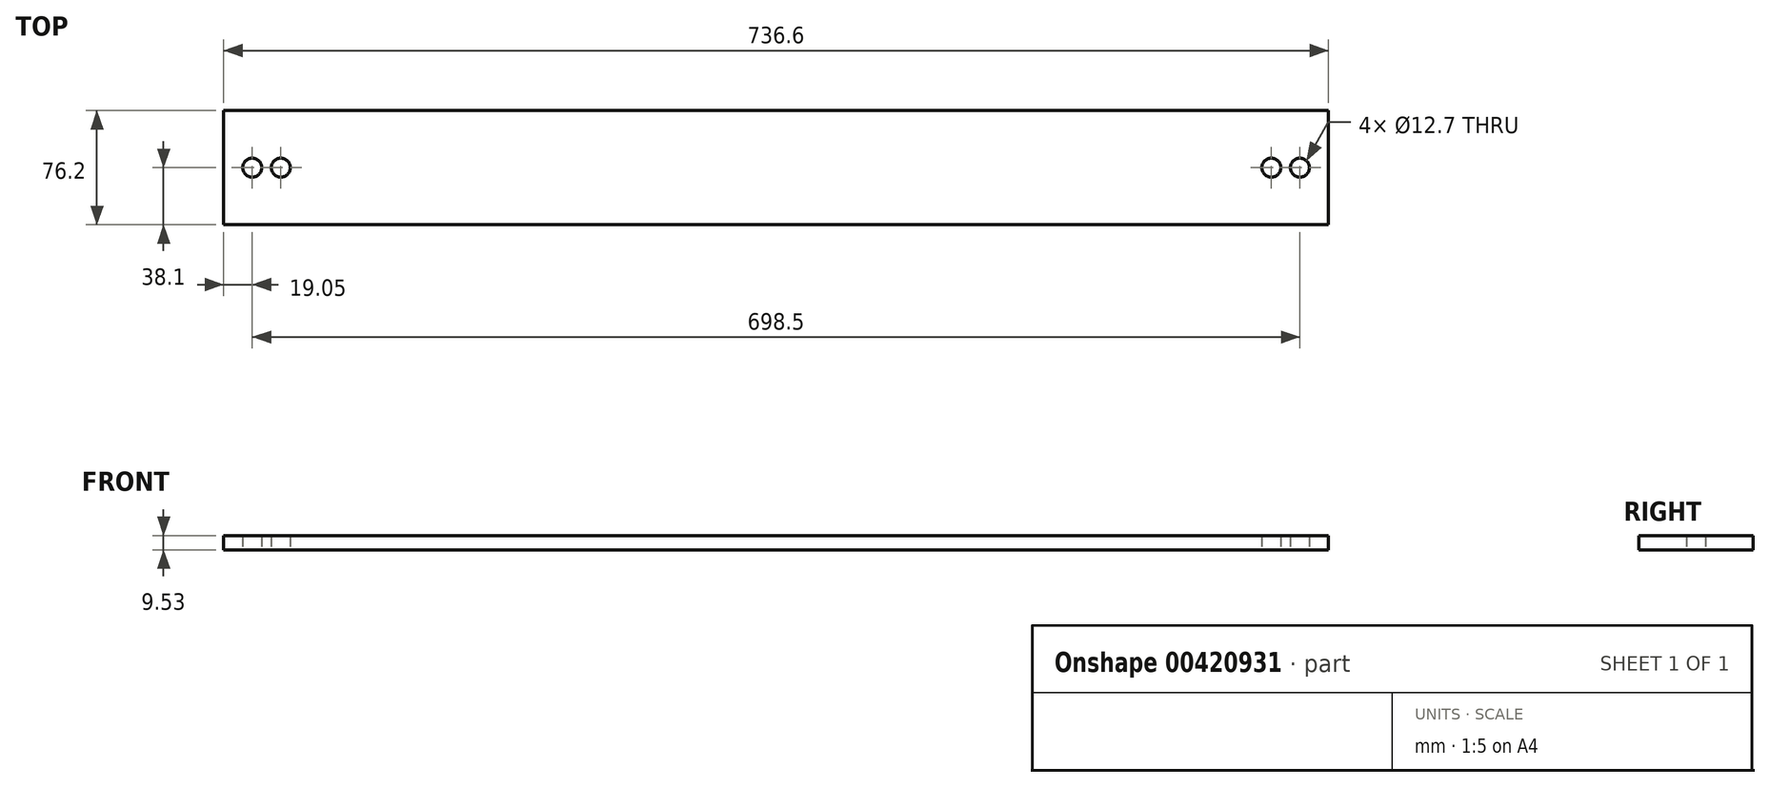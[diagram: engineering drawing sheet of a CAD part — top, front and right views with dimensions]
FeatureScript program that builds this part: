
annotation { "Feature Type Name" : "Feature", "Feature Type Description" : "" }
export const myFeature = defineFeature(function(context is Context, id is Id, definition is map)
    precondition{}
    {
        {
            var Q0;
            Q0=qCreatedBy(makeId("Top.planeOp"),FACE);
            var sketch = newSketch(context, id + "F0", { "sketchPlane" : qUnion([Q0])});
            skLineSegment(sketch, "E0.bottom", {"start": v(0, 0) * mm, "end": v(736.6, 0) * mm});
            skLineSegment(sketch, "E0.top", {"start": v(0, -76.2) * mm, "end": v(736.6, -76.2) * mm});
            skLineSegment(sketch, "E0.left", {"start": v(0, 0) * mm, "end": v(0, -76.2) * mm});
            skLineSegment(sketch, "E0.right", {"start": v(736.6, 0) * mm, "end": v(736.6, -76.2) * mm});
            skCircle(sketch, "E1", {"center": v(19.05, -38.1) * mm, "radius": 6.35 * mm});
            skCircle(sketch, "E2", {"center": v(38.1, -38.1) * mm, "radius": 6.35 * mm});
            skCircle(sketch, "E3", {"center": v(698.5, -38.1) * mm, "radius": 6.35 * mm});
            skCircle(sketch, "E4", {"center": v(717.55, -38.1) * mm, "radius": 6.35 * mm});
            skPoint(sketch, "E5", {"position": v(0, -38.1) * mm});
            skSolve(sketch);
        }
        {
            var Q0;
            Q0 = qSketchRegion(id + "F0", true);
            extrude(context, id + "F1", {"entities" : qUnion([Q0]), "depth" : 9.52 * mm});
        }
    });
